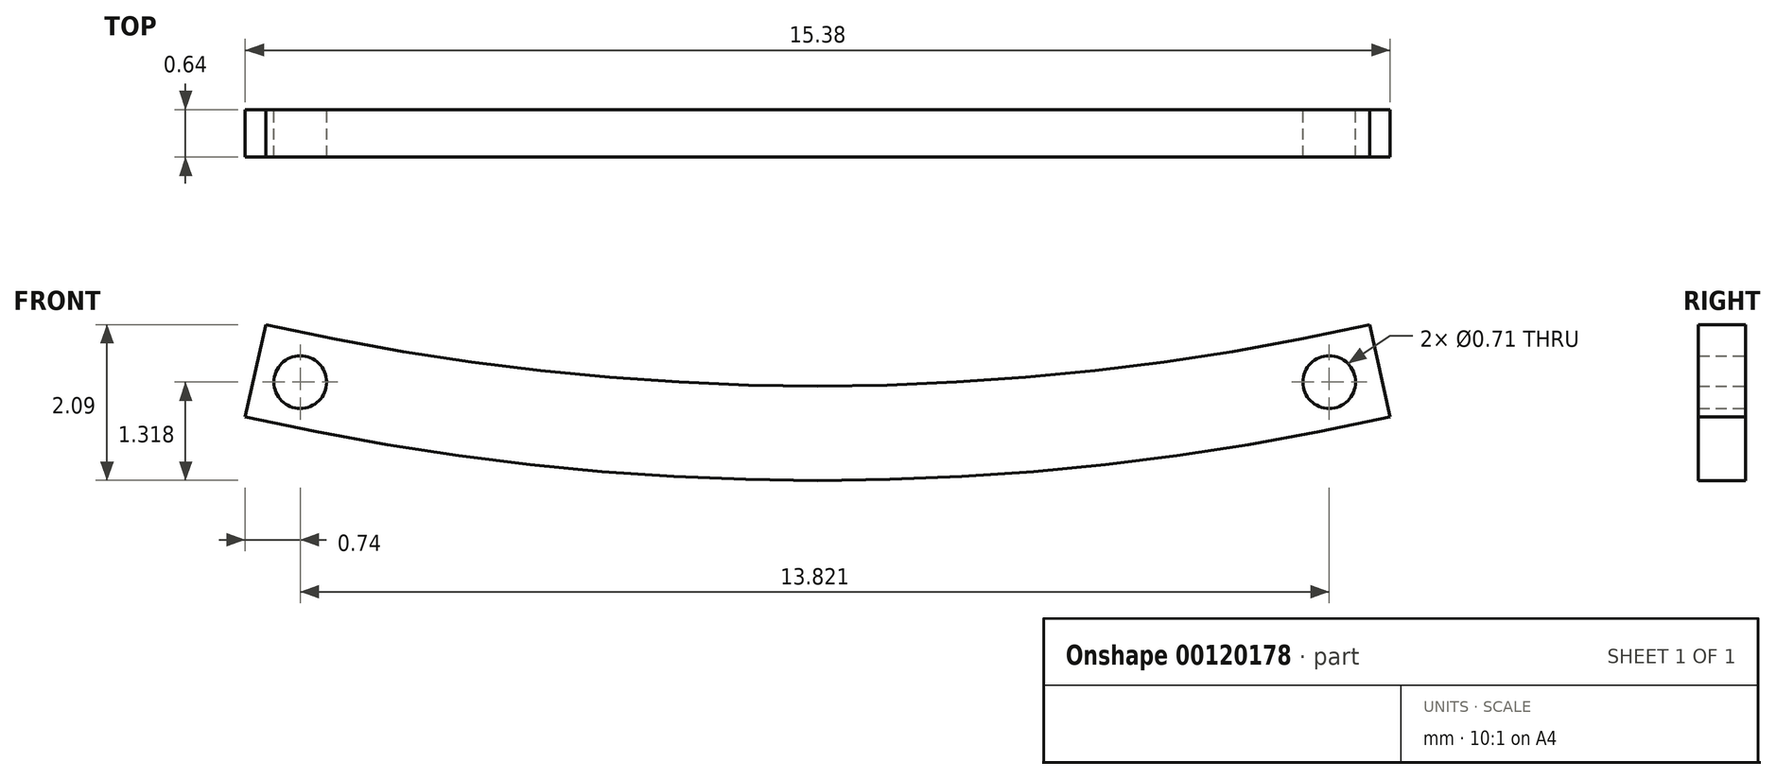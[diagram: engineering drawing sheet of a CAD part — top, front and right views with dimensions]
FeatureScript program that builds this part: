
annotation { "Feature Type Name" : "Feature", "Feature Type Description" : "" }
export const myFeature = defineFeature(function(context is Context, id is Id, definition is map)
    precondition{}
    {
        {
            var Q0;
            Q0=qCreatedBy(makeId("Front.planeOp"),FACE);
            var sketch = newSketch(context, id + "F0", { "sketchPlane" : qUnion([Q0])});
            skArc(sketch, "E0", {"start": v(-7.37, 0) * mm, "mid": v(0.04, -0.82) * mm, "end": v(7.45, 0) * mm});
            skArc(sketch, "E1.0", {"start": v(-7.65, -1.24) * mm, "mid": v(0.04, -2.1) * mm, "end": v(7.73, -1.24) * mm});
            skLineSegment(sketch, "E2", {"start": v(-7.65, -1.24) * mm, "end": v(-7.37, 0) * mm});
            skLineSegment(sketch, "E3", {"start": v(7.45, 0) * mm, "end": v(7.73, -1.24) * mm});
            skCircle(sketch, "E4", {"center": v(-6.91, -0.77) * mm, "radius": 0.35 * mm});
            skCircle(sketch, "E5.MirrorC", {"center": v(6.91, -0.77) * mm, "radius": 0.35 * mm});
            skSolve(sketch);
        }
        {
            var Q0;
            Q0=makeQuery(id+"F0.imprint","IMPRINT",FACE,{"disambiguationData":[TD([[makeQuery(id+"F0.imprint","IMPRINT",EDGE,{"derivedFrom":sQuery(id+"F0.wireOp",EDGE,"E0")}),-1.0]])]});
            extrude(context, id + "F1", {"entities" : qUnion([Q0]), "depth" : 0.64 * mm});
        }
    });
